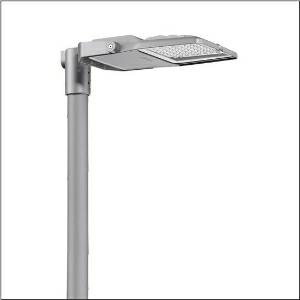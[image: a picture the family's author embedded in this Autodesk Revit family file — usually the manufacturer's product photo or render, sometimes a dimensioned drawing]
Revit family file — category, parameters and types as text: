
# Revit family: floodlight_fl_21_iq_mini___pl64_5xa7771d2e3a_d262
name_source: partatom
category: Lighting Fixtures
units: mm (PartAtom-declared; Revit-internal decimal feet)

## family parameters
Cut with Voids When Loaded = No
Host = Face
Light Source = No
Part Type = Normal
Room Calculation Point = No
Round Connector Dimension = Use Diameter
Shared = No

## types (1)
- --- (1 x LED, 17220 lm, 143 W, 3000K)
    Apparent Load = 143 VA
    CIE Flux Codes = 28 80 98 100 100
    Color Rendering = 70
    Color Temperature = 3000K
    Default Elevation = 1800 mm
    Description = Floodlight FL 21 iQ mini, floodlight, primary light control with lens, of PMMA, primary optical cover: protective disc, of toughened safety glass, transparent, light distribution: PL64, light emission: direct distribution, installation type: surface-mounted, LED, High Power LED, rated luminous flux: 17.220lm, luminous efficacy: 120lm/W, light colour: 730, colour temperature: 3000K, control gear: iQ Comfort/DALI, control: Auto-Match, Temp-Guard, Lumen-Switch, Night-Set, Smart-Wire, Light-Fading, Desk-Remote (wireless, voltage-free reading and setting of iQ features in the workshop via application-optimized NFC function/RFID function), optimised constant luminous flux control (CLO 2.0), with terminal, 6-pole, mains connection: 220..240V, AC, 50/60Hz, start of lifetime: 143W, end of service life: 152W, reduction: 61W, luminaire housing, of diecast aluminium, powder-coated, Siteco® metallic grey (DB 702S), corrosivity category C5 mid according to DIN EN ISO 12944, suitable for swimming pools, chlorine-resistant, sealing non-destructively replaceable, please order mast flange separately, mast bracket, of steel, galvanised, powder-coated, Siteco® metallic grey (DB 702S), protection rating (complete): IP66, insulation class (complete): insulation class II (safety insulation), certification: CE, ENEC, VDE, protection symbol: D, impact resistance: IK08, permissible operating ambient temperature: -40..+40°C, permissible operating ambient temperature for outdoor applications: -40..+50°C, standard: DIN EN 12944, LABS conformity tested according to VDMA 24364:2018-05, packaging unit: 1 piece

Light Distribution: PL64
    Height = 70 mm
    Lamp = 1 x LED
    Lamp Light Flux = 17220 lm
    Lamp Power = 143 W
    Lamp count = 1
    Length = 485 mm
    Luminous efficacy = 120 lm/W
    Manufacturer = Siteco
    ModVariant = No
    Model = 5XA7771D2E3A
    Number of Poles = 1
    OnlyDefault = Yes
    Power Factor = 1
    Product Name = Floodlight FL 21 iQ mini | PL64
    Product group = floodlight | pylon annexe
    ProductGroupID = 6200
    Protection Class = Protection class II
    Protection Degree = IP 66
    RLX_Detail_Level = 1
    RLX_Emergency_Light_Flux = 0 lm
    RLX_Emergency_Type = 0
    RLX_Emergency_Type_DB = No
    RlxData = <blob elided: 101577 chars, md5=7fcb1b1b>
    Socket = socket
    Standby Power = 0 W
    System Light Flux = 17220 lm
    System Power = 143 W
    Type Comments = factory setting: luminous flux: 100 % | dim-lin: 254 | 730 mA
    Type Image = l_1007125.jpg
    URL = http://relux.com
    VarID = @adj_166068
    Voltage = 0 V
    Weight = 0.00 kg
    Width = 337 mm

## geometry (parser evidence)
native form markers: Blend x4, Sweep x11
no freeform markers — native parametric forms only
